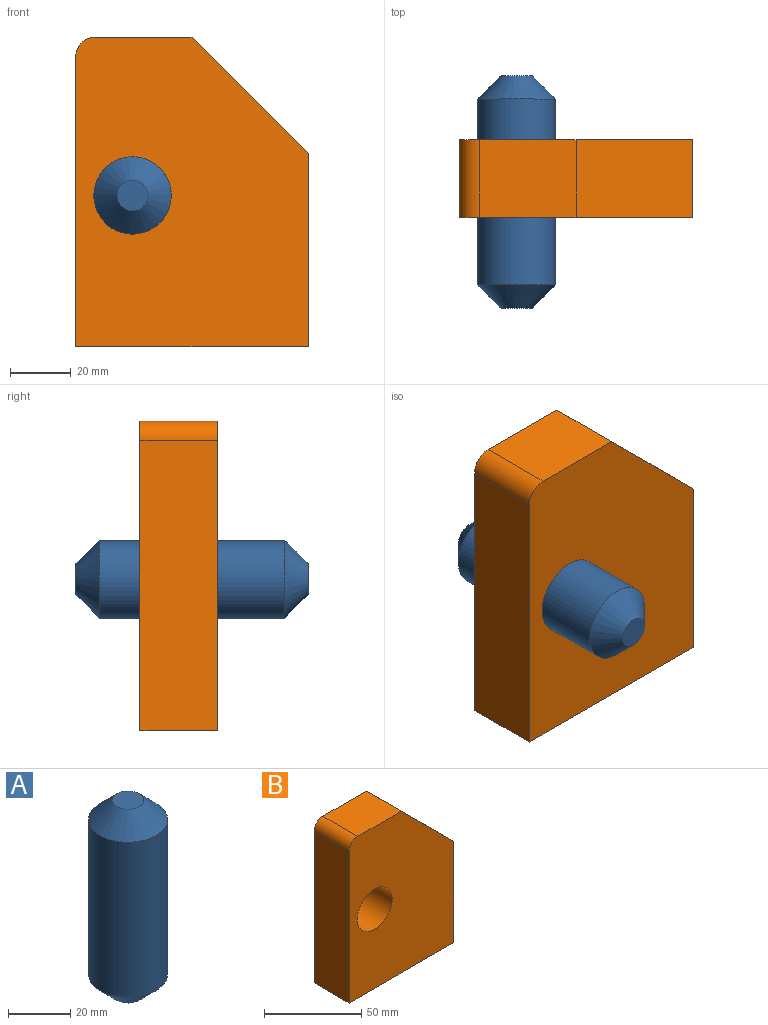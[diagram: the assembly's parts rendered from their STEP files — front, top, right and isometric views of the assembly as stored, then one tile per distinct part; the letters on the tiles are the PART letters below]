
ASSEMBLY  parts=2 mates=1
PART A: 5 faces, bbox 25.4x25.4x76.2 mm
  f0: cylinder r=12.7mm len=60.96mm, axis (0,0,-1), area 4864.4mm2, adj f3,f4
  f1: plane 10.16x10.16mm, normal (0,0,1), area 81.1mm2, adj f3
  f2: plane 10.16x10.16mm, normal (0,0,-1), area 81.1mm2, adj f4
  f3: cone r=5.08mm half-angle=45deg, axis (0,0,-1), area 601.9mm2, adj f0,f1
  f4: cone r=12.7mm half-angle=45deg, axis (0,0,1), area 601.9mm2, adj f0,f2
PART B: 9 faces, bbox 76.2x25.4x101.6 mm
  f0: plane 31.75x25.4mm, normal (0,0,1), area 806.5mm2, adj f5,f6,f7,f8
  f1: plane 95.25x25.4mm, normal (-1,0,0), area 2419.3mm2, adj f2,f5,f6,f8
  f2: plane 76.2x25.4mm, normal (0,0,-1), area 1935.5mm2, adj f1,f4,f5,f6
  f3: cylinder r=12.7mm len=25.4mm, axis (0,1,0), area 2026.8mm2, adj f5,f6
  f4: plane 63.5x25.4mm, normal (1,0,0), area 1612.9mm2, adj f2,f5,f6,f7
  f5: plane 101.6x76.2mm, normal (0,-1,0), area 6500.8mm2, adj f0,f1,f2,f3,f4,f7,f8
  f6: plane 101.6x76.2mm, normal (0,1,0), area 6500.8mm2, adj f0,f1,f2,f3,f4,f7,f8
  f7: plane 38.1x38.1mm, normal (0.71,0,0.71), area 1368.6mm2, adj f0,f4,f5,f6
  f8: cylinder r=6.35mm len=25.4mm, axis (0,-1,0), area 253.4mm2, adj f0,f1,f5,f6
PLACE A rot(axis=(1,0,0),90deg) t=(1.92,7.97,-47.83)mm
PLACE B t=(8.17,-13.07,6.66)mm fixed
MATE slider B.f3 <-> A.f0  axis (0,1,0) through (-50.37,-25.77,6.66)mm
